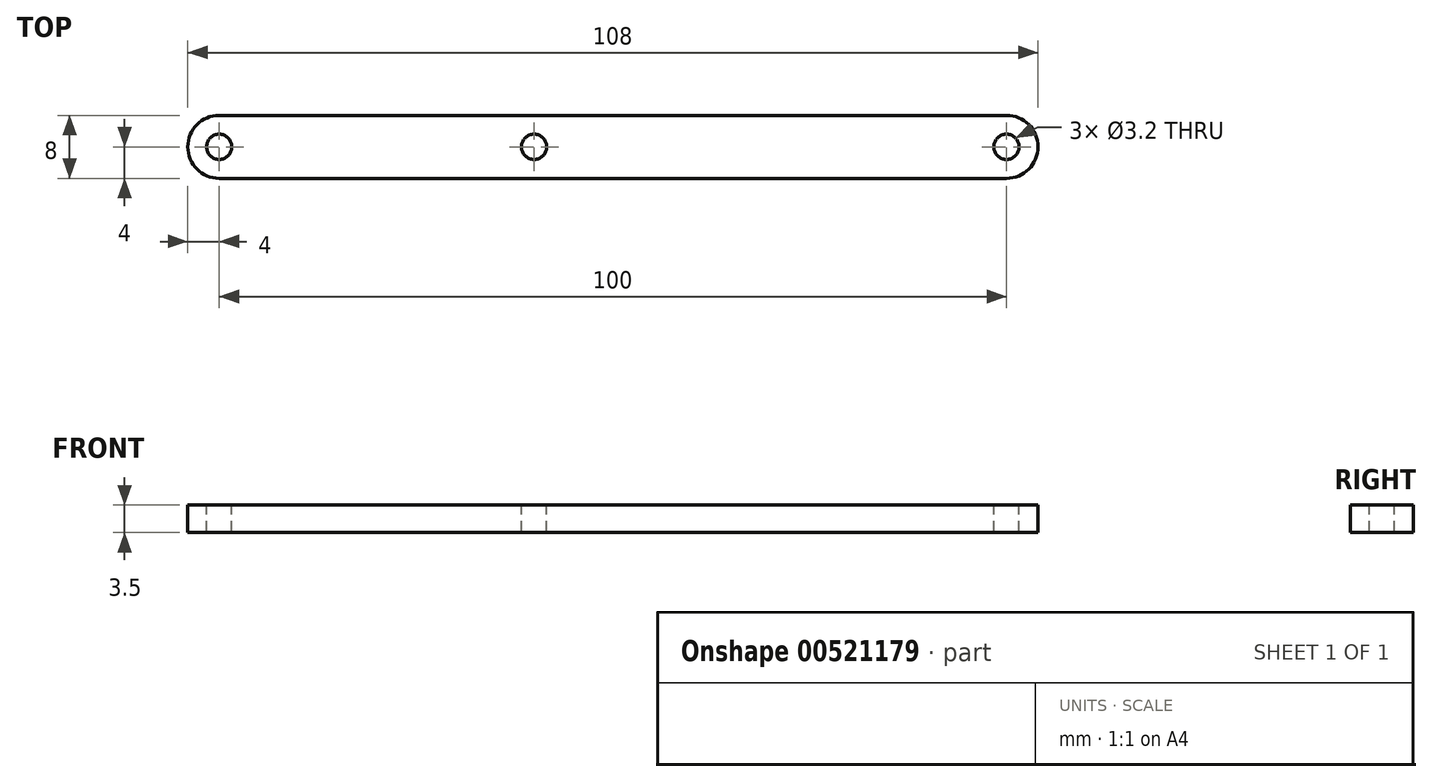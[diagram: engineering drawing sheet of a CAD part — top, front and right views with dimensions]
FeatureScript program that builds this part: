
annotation { "Feature Type Name" : "Feature", "Feature Type Description" : "" }
export const myFeature = defineFeature(function(context is Context, id is Id, definition is map)
    precondition{}
    {
        {
            var Q0;
            Q0=qCreatedBy(makeId("Top.planeOp"),FACE);
            var sketch = newSketch(context, id + "F0", { "sketchPlane" : qUnion([Q0])});
            skLineSegment(sketch, "E0.bottom", {"start": v(50, -4) * mm, "end": v(-50, -4) * mm});
            skLineSegment(sketch, "E0.top", {"start": v(50, 4) * mm, "end": v(-50, 4) * mm});
            skLineSegment(sketch, "E0.left", {"start": v(50, -4) * mm, "end": v(50, 4) * mm});
            skLineSegment(sketch, "E0.right", {"start": v(-50, -4) * mm, "end": v(-50, 4) * mm});
            skPoint(sketch, "E0.middle", {"position": v(0, 0) * mm});
            skCircle(sketch, "E1", {"center": v(-50, 0) * mm, "radius": 4 * mm});
            skCircle(sketch, "E2", {"center": v(50, 0) * mm, "radius": 4 * mm});
            skSolve(sketch);
        }
        {
            var Q0;
            Q0 = qSketchRegion(id + "F0", true);
            extrude(context, id + "F1", {"entities" : qUnion([Q0]), "depth" : 3.5 * mm, "offsetDistance" : 25 * mm});
        }
        {
            var Q0;
            Q0=makeQuery(id+"F1.opExtrude","CAP_FACE",FACE,{"disambiguationData":[OSD([sQuery(id+"F0.wireOp",EDGE,"E0.bottom"),sQuery(id+"F0.wireOp",EDGE,"E0.top"),sQuery(id+"F0.wireOp",EDGE,"E1"),sQuery(id+"F0.wireOp",EDGE,"E2")])],"isStart":false});
            var sketch = newSketch(context, id + "F2", { "sketchPlane" : qUnion([Q0])});
            skLineSegment(sketch, "E3.bottom", {"start": v(-50, 4) * mm, "end": v(50, 4) * mm});
            skLineSegment(sketch, "E3.top", {"start": v(-50, -4) * mm, "end": v(50, -4) * mm});
            skLineSegment(sketch, "E3.left", {"start": v(-50, 4) * mm, "end": v(-50, -4) * mm});
            skLineSegment(sketch, "E3.right", {"start": v(50, 4) * mm, "end": v(50, -4) * mm});
            skCircle(sketch, "E4", {"center": v(-50, 0) * mm, "radius": 1.6 * mm});
            skCircle(sketch, "E5", {"center": v(50, 0) * mm, "radius": 1.6 * mm});
            skLineSegment(sketch, "E6", {"start": v(-50, 0) * mm, "end": v(-10, 0) * mm});
            skCircle(sketch, "E7", {"center": v(-10, 0) * mm, "radius": 1.6 * mm});
            skSolve(sketch);
        }
        {
            var Q0;
            {var subQ0=sQuery(id+"F2.wireOp",EDGE,"E6");var subQ1=sQuery(id+"F2.wireOp",EDGE,"E3.left");var subQ2=makeQuery(id+"F2.imprint","INTERSECT",VERTEX,{"derivedFrom":[subQ1,subQ0]});Q0=makeQuery(id+"F2.imprint","IMPRINT",FACE,{"disambiguationData":[TD([[makeQuery(id+"F2.imprint","IMPRINT",EDGE,{"disambiguationData":[TD([[subQ2,1.0]])],"derivedFrom":subQ1}),1.0]])]});}
            var Q1;
            {var subQ0=sQuery(id+"F2.wireOp",EDGE,"E3.left");var subQ1=makeQuery(id+"F2.imprint","INTERSECT",VERTEX,{"derivedFrom":[subQ0,sQuery(id+"F2.wireOp",EDGE,"E6")]});Q1=makeQuery(id+"F2.imprint","IMPRINT",FACE,{"disambiguationData":[TD([[makeQuery(id+"F2.imprint","IMPRINT",EDGE,{"disambiguationData":[TD([[subQ1,1.0]])],"derivedFrom":subQ0}),-1.0]])]});}
            var Q2;
            Q2=makeQuery(id+"F2.imprint","IMPRINT",FACE,{"disambiguationData":[TD([[makeQuery(id+"F2.imprint","IMPRINT",EDGE,{"derivedFrom":sQuery(id+"F2.wireOp",EDGE,"E7")}),1.0]])]});
            var Q3;
            {var subQ0=sQuery(id+"F2.wireOp",EDGE,"E5");var subQ1=sQuery(id+"F2.wireOp",EDGE,"E3.right");var subQ2=makeQuery(id+"F2.imprint","INTERSECT",VERTEX,{"disambiguationData":[OD(0.0)],"derivedFrom":[subQ1,subQ0]});Q3=makeQuery(id+"F2.imprint","IMPRINT",FACE,{"disambiguationData":[TD([[makeQuery(id+"F2.imprint","IMPRINT",EDGE,{"disambiguationData":[TD([[subQ2,-1.0]])],"derivedFrom":subQ1}),-1.0]])]});}
            var Q4;
            {var subQ0=sQuery(id+"F2.wireOp",EDGE,"E5");var subQ1=sQuery(id+"F2.wireOp",EDGE,"E3.right");var subQ2=makeQuery(id+"F2.imprint","INTERSECT",VERTEX,{"disambiguationData":[OD(0.0)],"derivedFrom":[subQ1,subQ0]});Q4=makeQuery(id+"F2.imprint","IMPRINT",FACE,{"disambiguationData":[TD([[makeQuery(id+"F2.imprint","IMPRINT",EDGE,{"disambiguationData":[TD([[subQ2,-1.0]])],"derivedFrom":subQ1}),1.0]])]});}
            var Q5;
            {var subQ0=sQuery(id+"F2.wireOp",EDGE,"E6");var subQ1=sQuery(id+"F2.wireOp",EDGE,"E3.left");var subQ2=makeQuery(id+"F2.imprint","INTERSECT",VERTEX,{"derivedFrom":[subQ1,subQ0]});Q5=makeQuery(id+"F2.imprint","IMPRINT",FACE,{"disambiguationData":[TD([[makeQuery(id+"F2.imprint","IMPRINT",EDGE,{"disambiguationData":[TD([[subQ2,-1.0]])],"derivedFrom":subQ1}),1.0]])]});}
            extrude(context, id + "F3", {"entities" : qUnion([Q0, Q1, Q2, Q3, Q4, Q5]), "operationType" : NewBodyOperationType.REMOVE, "endBound" : BoundingType.THROUGH_ALL, "oppositeDirection" : true, "depth" : 25 * mm, "offsetDistance" : 25 * mm});
        }
    });
